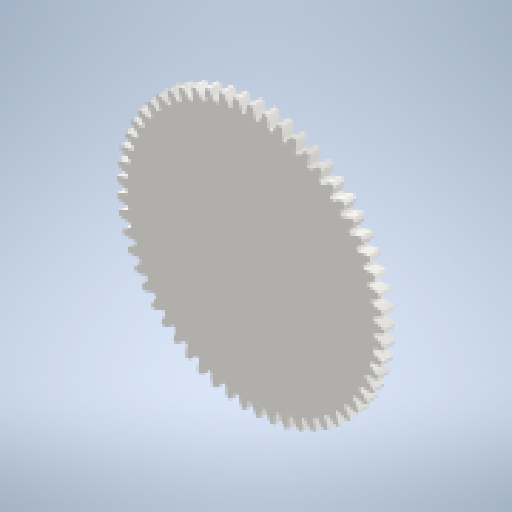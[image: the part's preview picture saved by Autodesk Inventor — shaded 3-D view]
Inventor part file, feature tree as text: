
AUTODESK INVENTOR PART (.ipt)
format: ipt  version: 2023 (Build 270158000, 158)  size: 553,984 bytes
history: native  units: mm (DEFAULTED — no unit token found)
features: plane x3, other x3, sketch x3, extrude x2, projected_geometry x1
ambient origin geometry x8: Origin, YZ Plane, XZ Plane, XY Plane, X Axis, Y Axis, Z Axis, Center Point
bodies: Solid1 (feature_tree)
feature tree (12):
  extrude  "Extrusion1"  Depth=5.0mm TaperAngle=0.0deg
  plane  "Work Plane2"
  plane  "Work Plane8"
  plane  "Work Plane9"
  other  "Spur Gear"
  extrude  "Extrusion2"  Depth=10.0mm TaperAngle=0.0deg
  sketch  "Sketch1"  dims[d0=118.0mm d1=5.0mm d2=0.0mm]
  sketch  "Sketch2"  dims[d3=114.0mm d4=10.0mm d5=0.0mm]
  other  "Srf1"
  sketch  "Sketch3"  dims[d16=80.0mm d17=0.0mm d34=0.551157mm d39=0.0mm d41=0.0mm d43=80.0mm d46=80.0mm d47=0.0mm d48=0.0mm d49=9.8mm d50=36.0mm d51=0.0mm]
  projected_geometry  "Projected Loop1"
  other  "Pitch Diameter"
